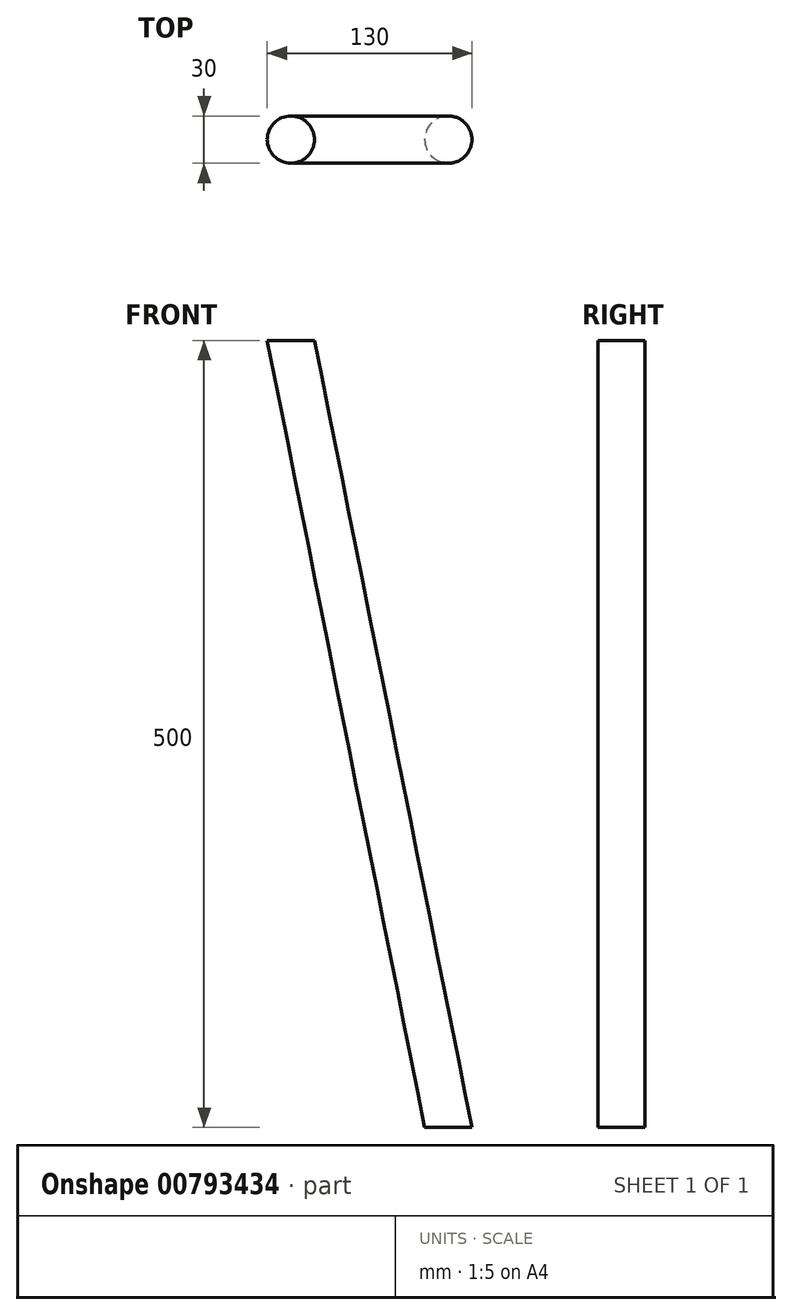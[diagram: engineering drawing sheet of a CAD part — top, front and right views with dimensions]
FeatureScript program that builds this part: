
annotation { "Feature Type Name" : "Feature", "Feature Type Description" : "" }
export const myFeature = defineFeature(function(context is Context, id is Id, definition is map)
    precondition{}
    {
        {
            var Q0;
            Q0=qCreatedBy(makeId("Front.planeOp"),FACE);
            var sketch = newSketch(context, id + "F0", { "sketchPlane" : qUnion([Q0])});
            skLineSegment(sketch, "E0", {"start": v(0, 361.8) * mm, "end": v(0, -138.2) * mm});
            skLineSegment(sketch, "E1", {"start": v(0, -138.2) * mm, "end": v(100, -138.2) * mm});
            skLineSegment(sketch, "E2", {"start": v(100, -138.2) * mm, "end": v(0, 361.8) * mm});
            skSolve(sketch);
        }
        {
            var Q0;
            Q0=qCreatedBy(makeId("Top.planeOp"),FACE);
            var sketch = newSketch(context, id + "F1", { "sketchPlane" : qUnion([Q0])});
            skCircle(sketch, "E3", {"center": v(0, 0) * mm, "radius": 15 * mm});
            skSolve(sketch);
        }
        {
            var Q0;
            Q0=makeQuery(id+"F1.imprint","IMPRINT",FACE,{"disambiguationData":[TD([[makeQuery(id+"F1.imprint","IMPRINT",EDGE,{"derivedFrom":sQuery(id+"F1.wireOp",EDGE,"E3")}),1.0]])]});
            var Q1;
            Q1=sQuery(id+"F0.wireOp",EDGE,"E2");
            sweep(context, id + "F2", {"profiles" : qUnion([Q0]), "path" : qUnion([Q1])});
        }
    });
